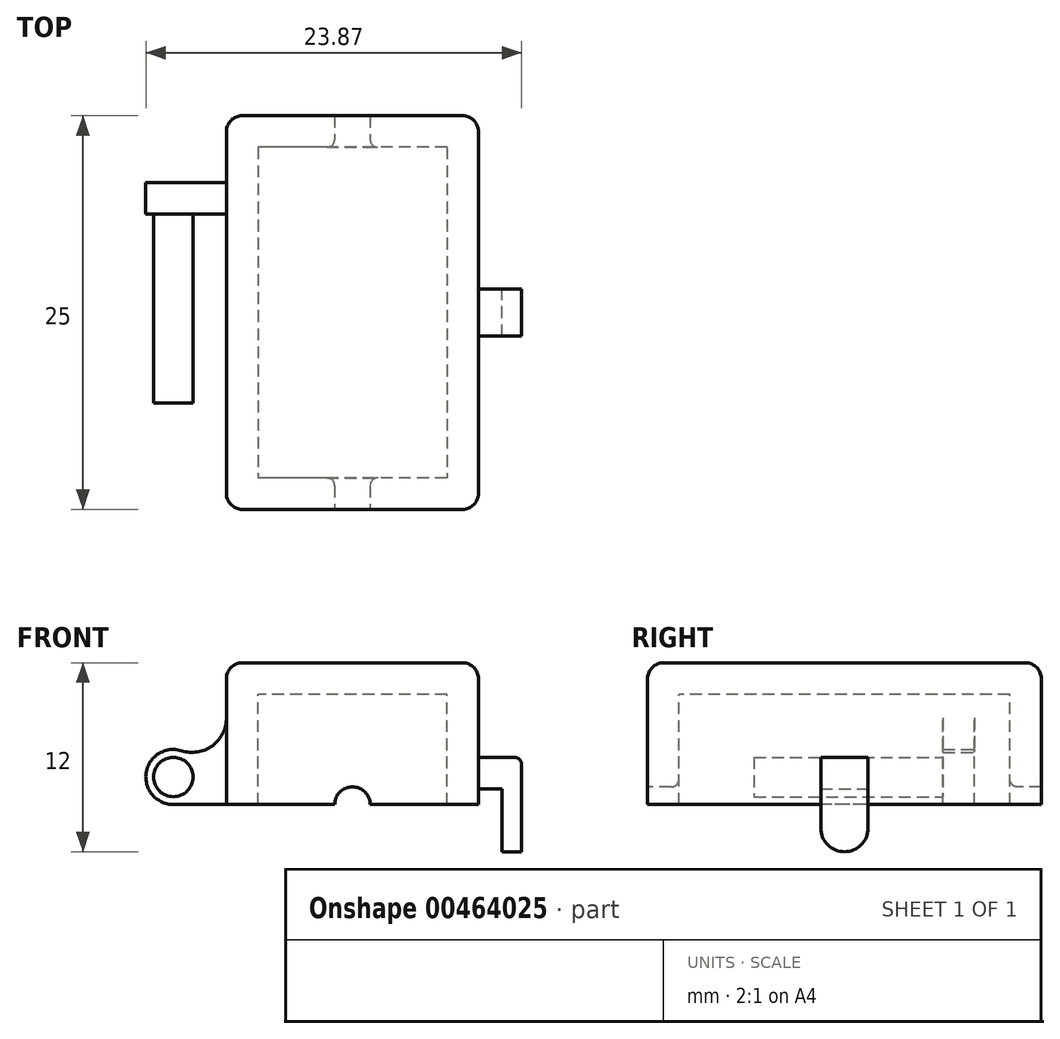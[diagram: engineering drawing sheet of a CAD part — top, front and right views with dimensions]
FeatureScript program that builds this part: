
annotation { "Feature Type Name" : "Feature", "Feature Type Description" : "" }
export const myFeature = defineFeature(function(context is Context, id is Id, definition is map)
    precondition{}
    {
        {
            var Q0;
            Q0=qCreatedBy(makeId("Top.planeOp"),FACE);
            var sketch = newSketch(context, id + "F0", { "sketchPlane" : qUnion([Q0])});
            skLineSegment(sketch, "E0.bottom", {"start": v(8, 12.5) * mm, "end": v(-8, 12.5) * mm});
            skLineSegment(sketch, "E0.top", {"start": v(8, -12.5) * mm, "end": v(-8, -12.5) * mm});
            skLineSegment(sketch, "E0.left", {"start": v(8, 12.5) * mm, "end": v(8, -12.5) * mm});
            skLineSegment(sketch, "E0.right", {"start": v(-8, 12.5) * mm, "end": v(-8, -12.5) * mm});
            skPoint(sketch, "E0.middle", {"position": v(0, 0) * mm});
            skSolve(sketch);
        }
        {
            var Q0;
            Q0=qSketchRegion(id+"F0",true);
            extrude(context, id + "F1", {"entities" : qUnion([Q0]), "oppositeDirection" : true, "depth" : 9 * mm});
        }
        {
            var Q0;
            Q0=makeQuery(id+"F1.opExtrude","CAP_FACE",FACE,{"disambiguationData":[OSD([sQuery(id+"F0.wireOp",EDGE,"E0.bottom"),sQuery(id+"F0.wireOp",EDGE,"E0.top"),sQuery(id+"F0.wireOp",EDGE,"E0.left"),sQuery(id+"F0.wireOp",EDGE,"E0.right")])],"isStart":false});
            shell(context, id + "F2", {"entities" : qUnion([Q0]), "thickness" : 2 * mm});
        }
        {
            var Q0;
            Q0=makeQuery(id+"F1.opExtrude","SWEPT_FACE",FACE,{"disambiguationData":[OSD([sQuery(id+"F0.wireOp",EDGE,"E0.bottom")])]});
            cPlane(context, id + "F3", {"entities" : qUnion([Q0]), "cplaneType" : CPlaneType.OFFSET, "offset" : (6 - 1.75) * mm, "oppositeDirection" : true, "width" : 150 * mm, "height" : 150 * mm});
        }
        {
            var Q0;
            Q0=qCreatedBy(id+"F3.planeOp",FACE);
            var sketch = newSketch(context, id + "F4", { "sketchPlane" : qUnion([Q0])});
            skArc(sketch, "E1", {"start": v(11.38, -9) * mm, "mid": v(13.1, -6.98) * mm, "end": v(10.85, -5.58) * mm});
            skLineSegment(sketch, "E2.0", {"start": v(8, -9) * mm, "end": v(8, -3.5) * mm});
            skArc(sketch, "E3", {"start": v(8, -3.5) * mm, "mid": v(8.9, -5.26) * mm, "end": v(10.85, -5.58) * mm});
            skLineSegment(sketch, "E4", {"start": v(10.85, -5.58) * mm, "end": v(10.85, -5.58) * mm});
            skLineSegment(sketch, "E5", {"start": v(8, -9) * mm, "end": v(11.38, -9) * mm});
            skSolve(sketch);
        }
        {
            var Q0;
            Q0 = qSketchRegion(id + "F4", true);
            extrude(context, id + "F5", {"entities" : qUnion([Q0]), "operationType" : NewBodyOperationType.ADD, "oppositeDirection" : true, "depth" : 2 * mm});
        }
        {
            var Q0;
            Q0=makeQuery(id+"F5.opExtrude","CAP_FACE",FACE,{"disambiguationData":[OSD([sQuery(id+"F4.wireOp",EDGE,"E1"),sQuery(id+"F4.wireOp",EDGE,"E2.0"),sQuery(id+"F4.wireOp",EDGE,"E3"),sQuery(id+"F4.wireOp",EDGE,"E5")])],"isStart":false});
            var sketch = newSketch(context, id + "F6", { "sketchPlane" : qUnion([Q0])});
            skCircle(sketch, "E6", {"center": v(-11.38, -7.25) * mm, "radius": 1.25 * mm});
            skSolve(sketch);
        }
        {
            var Q0;
            Q0=makeQuery(id+"F6.imprint","IMPRINT",FACE,{"disambiguationData":[TD([[makeQuery(id+"F6.imprint","IMPRINT",EDGE,{"derivedFrom":sQuery(id+"F6.wireOp",EDGE,"E6")}),1.0]])]});
            extrude(context, id + "F7", {"entities" : qUnion([Q0]), "operationType" : NewBodyOperationType.ADD, "depth" : 12 * mm});
        }
        {
            var Q0;
            Q0=makeQuery(id+"F1.opExtrude","CAP_EDGE",EDGE,{"disambiguationData":[OSD([sQuery(id+"F0.wireOp",EDGE,"E0.bottom")])],"isStart":true});
            var Q1;
            Q1=makeQuery(id+"F1.opExtrude","SWEPT_EDGE",EDGE,{"disambiguationData":[OSD([sQuery(id+"F0.wireOp",EDGE,"E0.bottom"),sQuery(id+"F0.wireOp",EDGE,"E0.right")])]});
            var Q2;
            Q2=makeQuery(id+"F1.opExtrude","CAP_EDGE",EDGE,{"disambiguationData":[OSD([sQuery(id+"F0.wireOp",EDGE,"E0.right")])],"isStart":true});
            var Q3;
            Q3=makeQuery(id+"F1.opExtrude","SWEPT_EDGE",EDGE,{"disambiguationData":[OSD([sQuery(id+"F0.wireOp",EDGE,"E0.top"),sQuery(id+"F0.wireOp",EDGE,"E0.right")])]});
            var Q4;
            Q4=makeQuery(id+"F1.opExtrude","CAP_EDGE",EDGE,{"disambiguationData":[OSD([sQuery(id+"F0.wireOp",EDGE,"E0.left")])],"isStart":true});
            var Q5;
            Q5=makeQuery(id+"F1.opExtrude","SWEPT_EDGE",EDGE,{"disambiguationData":[OSD([sQuery(id+"F0.wireOp",EDGE,"E0.bottom"),sQuery(id+"F0.wireOp",EDGE,"E0.left")])]});
            var Q6;
            Q6=makeQuery(id+"F1.opExtrude","SWEPT_EDGE",EDGE,{"disambiguationData":[OSD([sQuery(id+"F0.wireOp",EDGE,"E0.top"),sQuery(id+"F0.wireOp",EDGE,"E0.left")])]});
            var Q7;
            Q7=makeQuery(id+"F1.opExtrude","CAP_EDGE",EDGE,{"disambiguationData":[OSD([sQuery(id+"F0.wireOp",EDGE,"E0.top")])],"isStart":true});
            fillet(context, id + "F8", {"entities" : qUnion([Q0, Q1, Q2, Q3, Q4, Q5, Q6, Q7]), "radius" : 1 * mm, "tangentPropagation" : true, "allowEdgeOverflow" : false});
        }
        {
            var Q0;
            Q0=qCreatedBy(makeId("Front.planeOp"),FACE);
            var sketch = newSketch(context, id + "F9", { "sketchPlane" : qUnion([Q0])});
            skCircle(sketch, "E7", {"center": v(0, -9) * mm, "radius": 1.13 * mm});
            skSolve(sketch);
        }
        {
            var Q0;
            Q0 = qSketchRegion(id + "F9", true);
            extrude(context, id + "F10", {"entities" : qUnion([Q0]), "operationType" : NewBodyOperationType.REMOVE, "endBound" : BoundingType.SYMMETRIC, "oppositeDirection" : true, "depth" : 25 * mm});
        }
        {
            var Q0;
            Q0=qCreatedBy(makeId("Front.planeOp"),FACE);
            var sketch = newSketch(context, id + "F11", { "sketchPlane" : qUnion([Q0])});
            skLineSegment(sketch, "E8", {"start": v(10.75, -6) * mm, "end": v(10.75, -12) * mm});
            skLineSegment(sketch, "E9", {"start": v(10.75, -6) * mm, "end": v(8, -6) * mm});
            skLineSegment(sketch, "E10", {"start": v(9.5, -8) * mm, "end": v(9.5, -12) * mm});
            skLineSegment(sketch, "E11", {"start": v(10.75, -12) * mm, "end": v(9.5, -12) * mm});
            skLineSegment(sketch, "E12.0", {"start": v(8, -9) * mm, "end": v(8, -1) * mm});
            skLineSegment(sketch, "E13", {"start": v(9.5, -8) * mm, "end": v(8, -8) * mm});
            skPoint(sketch, "E14.orphan", {"position": v(8.25, -12) * mm});
            skSolve(sketch);
        }
        {
            var Q0;
            Q0 = qSketchRegion(id + "F11", true);
            extrude(context, id + "F12", {"entities" : qUnion([Q0]), "operationType" : NewBodyOperationType.ADD, "endBound" : BoundingType.SYMMETRIC, "depth" : 3 * mm});
        }
        {
            var Q0;
            Q0=makeQuery(id+"F12.opExtrude","SWEPT_FACE",FACE,{"disambiguationData":[OSD([sQuery(id+"F11.wireOp",EDGE,"E8")])]});
            var sketch = newSketch(context, id + "F13", { "sketchPlane" : qUnion([Q0])});
            skArc(sketch, "E15", {"start": v(-1.5, -10.5) * mm, "mid": v(0, -12) * mm, "end": v(1.5, -10.5) * mm});
            skLineSegment(sketch, "E16", {"start": v(-1.5, -10.5) * mm, "end": v(-1.5, -12) * mm});
            skLineSegment(sketch, "E17", {"start": v(-1.5, -12) * mm, "end": v(0, -12) * mm});
            skLineSegment(sketch, "E18", {"start": v(0, -12) * mm, "end": v(1.5, -12) * mm});
            skLineSegment(sketch, "E19", {"start": v(1.5, -12) * mm, "end": v(1.5, -10.5) * mm});
            skSolve(sketch);
        }
        {
            var Q0;
            Q0 = qSketchRegion(id + "F13", true);
            extrude(context, id + "F14", {"entities" : qUnion([Q0]), "operationType" : NewBodyOperationType.REMOVE, "oppositeDirection" : true, "depth" : 5 * mm});
        }
        {
            var Q0;
            Q0=makeQuery(id+"F12.opExtrude","SWEPT_EDGE",EDGE,{"disambiguationData":[OSD([sQuery(id+"F11.wireOp",EDGE,"E8"),sQuery(id+"F11.wireOp",EDGE,"E9")])]});
            fillet(context, id + "F15", {"entities" : qUnion([Q0]), "radius" : .5 * mm, "tangentPropagation" : true, "allowEdgeOverflow" : false});
        }
        {
            var Q0;
            Q0=makeQuery(id+"F7.opExtrude","CAP_EDGE",EDGE,{"disambiguationData":[OSD([sQuery(id+"F6.wireOp",EDGE,"E6")])],"isStart":true});
            var Q1;
            Q1=makeQuery(id+"F10.boolean.opBoolean","COPY",EDGE,{"derivedFrom":makeQuery(id+"F10.opExtrude","CAP_EDGE",EDGE,{"disambiguationData":[OSD([sQuery(id+"F9.wireOp",EDGE,"E7")])],"isStart":true})});
            var Q2;
            Q2=makeQuery(id+"F10.boolean.opBoolean","INTERSECT",EDGE,{"derivedFrom":[makeQuery(id+"F2.opShell","OFFSET_FACE",FACE,{"disambiguationData":[OSD([sQuery(id+"F0.wireOp",EDGE,"E0.top")])]}),makeQuery(id+"F10.opExtrude","SWEPT_FACE",FACE,{"disambiguationData":[OSD([sQuery(id+"F9.wireOp",EDGE,"E7")])]})]});
            var Q3;
            Q3=makeQuery(id+"F10.boolean.opBoolean","COPY",EDGE,{"derivedFrom":makeQuery(id+"F10.opExtrude","CAP_EDGE",EDGE,{"disambiguationData":[OSD([sQuery(id+"F9.wireOp",EDGE,"E7")])],"isStart":false})});
            var Q4;
            Q4=makeQuery(id+"F10.boolean.opBoolean","INTERSECT",EDGE,{"derivedFrom":[makeQuery(id+"F2.opShell","OFFSET_FACE",FACE,{"disambiguationData":[OSD([sQuery(id+"F0.wireOp",EDGE,"E0.bottom")])]}),makeQuery(id+"F10.opExtrude","SWEPT_FACE",FACE,{"disambiguationData":[OSD([sQuery(id+"F9.wireOp",EDGE,"E7")])]})]});
            fillet(context, id + "F16", {"entities" : qUnion([Q0, Q1, Q2, Q3, Q4]), "radius" : .5 * mm, "tangentPropagation" : true, "allowEdgeOverflow" : false});
        }
    });
